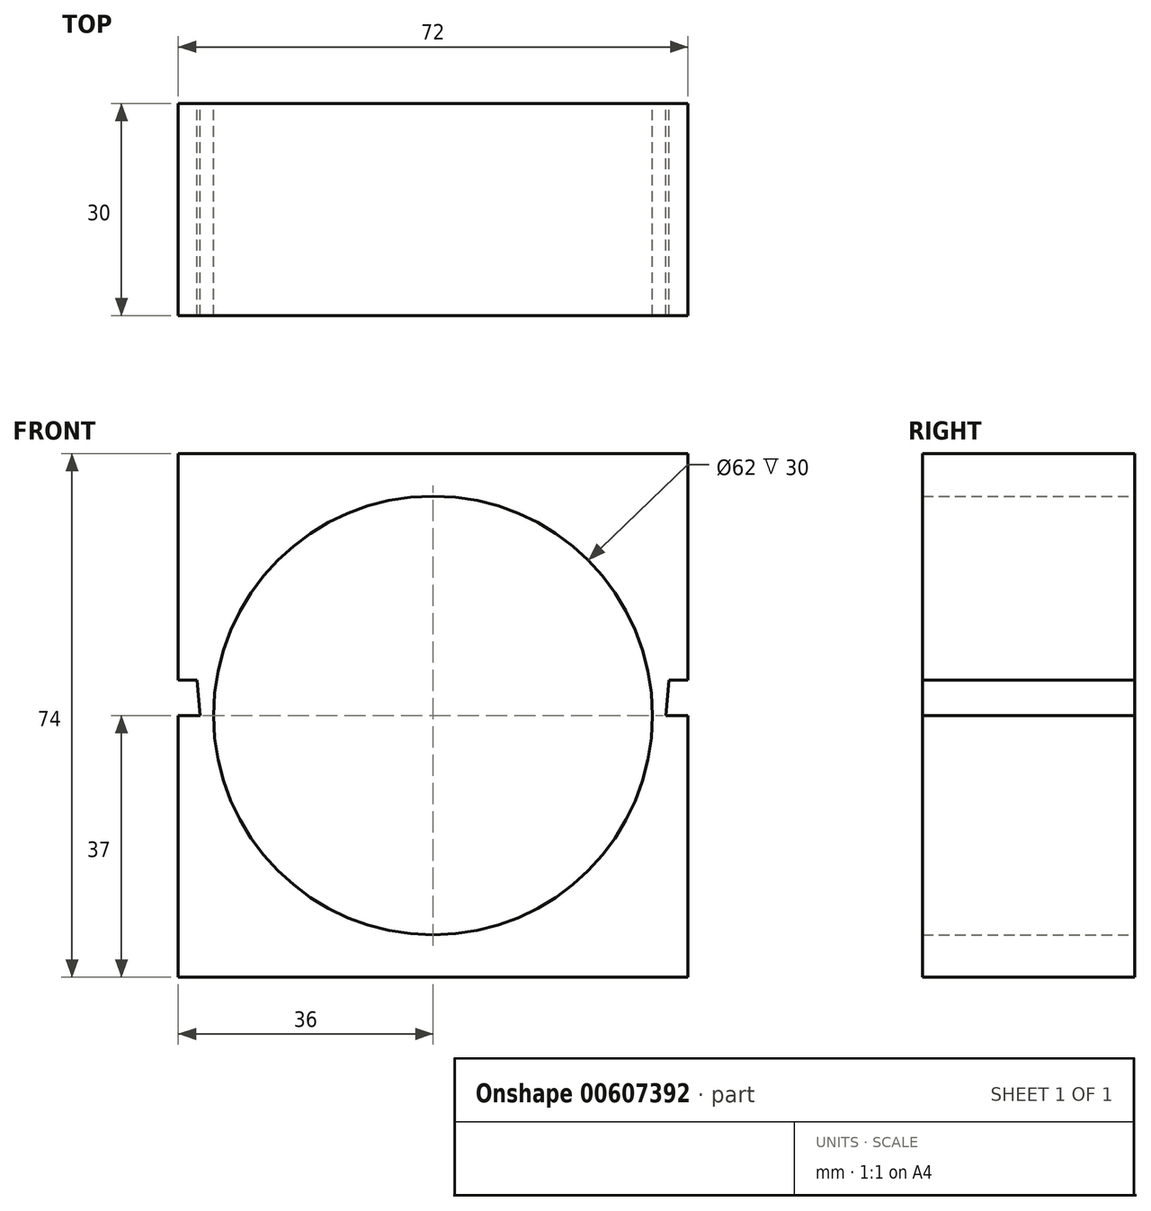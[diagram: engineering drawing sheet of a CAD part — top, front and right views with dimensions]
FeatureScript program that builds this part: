
annotation { "Feature Type Name" : "Feature", "Feature Type Description" : "" }
export const myFeature = defineFeature(function(context is Context, id is Id, definition is map)
    precondition{}
    {
        {
            var Q0;
            Q0=qCreatedBy(makeId("Front.planeOp"),FACE);
            var sketch = newSketch(context, id + "F0", { "sketchPlane" : qUnion([Q0])});
            skArc(sketch, "E0", {"start": v(-31, 0) * mm, "mid": v(0, -31) * mm, "end": v(31, 0) * mm});
            skLineSegment(sketch, "E1", {"start": v(-31, 0) * mm, "end": v(-36, 0) * mm});
            skLineSegment(sketch, "E2", {"start": v(-36, 0) * mm, "end": v(-36, -37) * mm});
            skLineSegment(sketch, "E3", {"start": v(-36, -37) * mm, "end": v(36, -37) * mm});
            skLineSegment(sketch, "E4", {"start": v(36, -37) * mm, "end": v(36, 0) * mm});
            skLineSegment(sketch, "E5", {"start": v(36, 0) * mm, "end": v(31, 0) * mm});
            skSolve(sketch);
        }
        {
            var Q0;
            Q0 = qSketchRegion(id + "F0", true);
            extrude(context, id + "F1", {"entities" : qUnion([Q0]), "depth" : 30 * mm, "offsetDistance" : 25 * mm});
        }
        {
            var Q0;
            Q0=makeQuery(id+"F1.opExtrude","SWEPT_BODY",BODY,{"disambiguationData":[OSD([sQuery(id+"F0.wireOp",EDGE,"E0"),sQuery(id+"F0.wireOp",EDGE,"E1"),sQuery(id+"F0.wireOp",EDGE,"E2"),sQuery(id+"F0.wireOp",EDGE,"E3"),sQuery(id+"F0.wireOp",EDGE,"E4"),sQuery(id+"F0.wireOp",EDGE,"E5")])]});
            transform(context, id + "F2", {"entities" : qUnion([Q0]), "transformType" : TransformType.TRANSLATION_3D, "dx" : 0 * mm, "dy" : 0 * mm, "dz" : 37 * mm, "makeCopy" : true});
        }
        {
            var Q0;
            Q0=qCreatedBy(makeId("Top.planeOp"),FACE);
            cPlane(context, id + "F3", {"entities" : qUnion([Q0]), "cplaneType" : CPlaneType.OFFSET, "offset" : 37 / 2 * mm, "width" : 150 * mm, "height" : 150 * mm});
        }
        {
            var Q0;
            Q0=qCreatedBy(id+"F3.planeOp",FACE);
            var sketch = newSketch(context, id + "F4", { "sketchPlane" : qUnion([Q0])});
            skLineSegment(sketch, "E6", {"start": v(0, -46.75) * mm, "end": v(0, 26.77) * mm, "construction": true});
            skSolve(sketch);
        }
        {
            var Q0;
            Q0=makeQuery(id+"F2.opPattern","COPY",BODY,{"derivedFrom":makeQuery(id+"F1.opExtrude","SWEPT_BODY",BODY,{"disambiguationData":[OSD([sQuery(id+"F0.wireOp",EDGE,"E0"),sQuery(id+"F0.wireOp",EDGE,"E1"),sQuery(id+"F0.wireOp",EDGE,"E2"),sQuery(id+"F0.wireOp",EDGE,"E3"),sQuery(id+"F0.wireOp",EDGE,"E4"),sQuery(id+"F0.wireOp",EDGE,"E5")])]}),"instanceName":"1"});
            var Q1;
            Q1=sQuery(id+"F4.wireOp",EDGE,"E6");
            transform(context, id + "F5", {"entities" : qUnion([Q0]), "transformType" : TransformType.ROTATION, "transformAxis" : qUnion([Q1]), "angle" : 180 * degree, "makeCopy" : false});
        }
        {
            var Q0;
            Q0=makeQuery(id+"F1.opExtrude","CAP_FACE",FACE,{"disambiguationData":[OSD([sQuery(id+"F0.wireOp",EDGE,"E0"),sQuery(id+"F0.wireOp",EDGE,"E1"),sQuery(id+"F0.wireOp",EDGE,"E2"),sQuery(id+"F0.wireOp",EDGE,"E3"),sQuery(id+"F0.wireOp",EDGE,"E4"),sQuery(id+"F0.wireOp",EDGE,"E5")])],"isStart":true});
            var sketch = newSketch(context, id + "F6", { "sketchPlane" : qUnion([Q0])});
            skLineSegment(sketch, "E7", {"start": v(-36, 0) * mm, "end": v(-36, 5) * mm});
            skLineSegment(sketch, "E8", {"start": v(-36, 5) * mm, "end": v(-33.74, 5) * mm});
            skLineSegment(sketch, "E9", {"start": v(-33.74, 5) * mm, "end": v(-33.3, 0) * mm});
            skLineSegment(sketch, "E10", {"start": v(-33.3, 0) * mm, "end": v(-36, 0) * mm});
            skLineSegment(sketch, "E11.MirrorCS", {"start": v(36, 5) * mm, "end": v(33.74, 5) * mm});
            skLineSegment(sketch, "E12.MirrorCS", {"start": v(36, 0) * mm, "end": v(36, 5) * mm});
            skLineSegment(sketch, "E13.MirrorCS", {"start": v(33.74, 5) * mm, "end": v(33.3, 0) * mm});
            skLineSegment(sketch, "E14.MirrorCS", {"start": v(33.3, 0) * mm, "end": v(36, 0) * mm});
            skSolve(sketch);
        }
        {
            var Q0;
            Q0 = qSketchRegion(id + "F6", true);
            var Q1;
            Q1=makeQuery(id+"F1.opExtrude","CAP_FACE",FACE,{"disambiguationData":[OSD([sQuery(id+"F0.wireOp",EDGE,"E0"),sQuery(id+"F0.wireOp",EDGE,"E1"),sQuery(id+"F0.wireOp",EDGE,"E2"),sQuery(id+"F0.wireOp",EDGE,"E3"),sQuery(id+"F0.wireOp",EDGE,"E4"),sQuery(id+"F0.wireOp",EDGE,"E5")])],"isStart":false});
            extrude(context, id + "F7", {"entities" : qUnion([Q0]), "operationType" : NewBodyOperationType.ADD, "endBound" : BoundingType.UP_TO_SURFACE, "oppositeDirection" : true, "depth" : 25 * mm, "endBoundEntityFace" : qUnion([Q1]), "offsetDistance" : 25 * mm});
        }
        {
            var Q0;
            Q0=makeQuery(id+"F2.opPattern","COPY",FACE,{"derivedFrom":makeQuery(id+"F1.opExtrude","CAP_FACE",FACE,{"disambiguationData":[OSD([sQuery(id+"F0.wireOp",EDGE,"E0"),sQuery(id+"F0.wireOp",EDGE,"E1"),sQuery(id+"F0.wireOp",EDGE,"E2"),sQuery(id+"F0.wireOp",EDGE,"E3"),sQuery(id+"F0.wireOp",EDGE,"E4"),sQuery(id+"F0.wireOp",EDGE,"E5")])],"isStart":true}),"instanceName":"1"});
            var sketch = newSketch(context, id + "F8", { "sketchPlane" : qUnion([Q0])});
            skLineSegment(sketch, "E15", {"start": v(-33.34, 5.01) * mm, "end": v(-32.9, 0) * mm});
            skLineSegment(sketch, "E16", {"start": v(-33.34, 5.01) * mm, "end": v(-36, 5.01) * mm});
            skLineSegment(sketch, "E17", {"start": v(-36, 5.01) * mm, "end": v(-36, 0) * mm});
            skLineSegment(sketch, "E18", {"start": v(-36, 0) * mm, "end": v(-32.9, 0) * mm});
            skLineSegment(sketch, "E19.MirrorCS", {"start": v(33.34, 5.01) * mm, "end": v(32.9, 0) * mm});
            skLineSegment(sketch, "E20.MirrorCS", {"start": v(36, 5.01) * mm, "end": v(36, 0) * mm});
            skLineSegment(sketch, "E21.MirrorCS", {"start": v(33.34, 5.01) * mm, "end": v(36, 5.01) * mm});
            skLineSegment(sketch, "E22.MirrorCS", {"start": v(36, 0) * mm, "end": v(32.9, 0) * mm});
            skSolve(sketch);
        }
        {
            var Q0;
            Q0 = qSketchRegion(id + "F8", true);
            extrude(context, id + "F9", {"entities" : qUnion([Q0]), "operationType" : NewBodyOperationType.REMOVE, "endBound" : BoundingType.UP_TO_NEXT, "oppositeDirection" : true, "depth" : 25 * mm, "offsetDistance" : 25 * mm});
        }
    });
